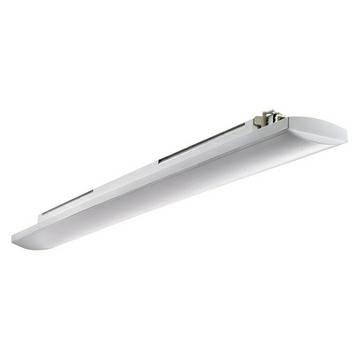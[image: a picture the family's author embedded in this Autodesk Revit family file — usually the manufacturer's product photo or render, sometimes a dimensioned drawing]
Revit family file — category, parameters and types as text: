
# Revit family: Lighting-Industriale-GEWISS-SMART[3]PLUS-PLAFONIERA-LED-EMERGENZA_OPALE_1600mm
name_source: partatom
category: Apparecchi per illuminazione
units: mm (PartAtom-declared; Revit-internal decimal feet)

## family parameters
Condiviso = No
Host = Superficie
Numero OmniClass = 23.80.70.11
Punto di calcolo locali = No
Quota connettore circolare = Usa diametro
Sorgente d'illuminazione = No
Taglio con vuoti quando caricato = No
Tipo di parte = Normale
Titolo OmniClass = Luminaries for Internal Lighting

## types (1)
- Lighting-Industriale-GEWISS-SMART[3]PLUS-PLAFONIERA-LED-EMERGENZA_OPALE_1600mm
    Applicazione = Interno
    Carico apparente = 55 VA
    Catalogo = LIGHTING
    Catalogo Serie = SMART[3] PLUS
    Classe di efficienza LED integrati = A ÷ A++
    Classe isolamento = II
    Codice Electrocod = 2434
    Commenti sul wattaggio = 55W
    Descrizione = SMART3 PLUS 1600 EMERG DT1+DT6 HE OPAL 9 57
    Ganci = GEWISS  - ALLUMINIO
    Garanzia = ND
    Glow Wire Test = 850°C
    Grado di protezione = IP66/IP69
    IDF = 85711e4a-cc34-4edf-afe5-693d24e48af9
    IDT = fc3a2e1b-6a5f-4da6-a0ae-96bfc5d9bbbb
    Immagine tipo = GWS3158P.jpg
    Lampada = LED
    Lampada: = LED
    Lumen output (lm) = 5200
    Lunghezza = 1600 mm
    Lunghezza Lampada = 1600 mm  [stored 5.24934 ft]
    Modello = GWS3325AP957
    Potenza di sistema = 50 W
    Produttore = GEWISS S.p.A.
    Prospetto di default = 1219 mm
    Resistenza agli urti = IK08
    SEO = Plafoniera
    Scheda Tecnica = https://www.gewiss.com
    Schermo = Opale
    Schermo. = Gewiss - Led Acceso
    Stampa 1_100 = Sì
    Stampa 1_200 = No
    Struttura = GEWISS - SMART 3 - GRIGIO
    Temperatura di colore = 5700 K (CRI > 90)
    Temperatura di colore: = 5700 K (CRI > 90)
    Temperatura di funzionamento = ND
    Temperatura di utilizzo = ND
    Tensione = 220-240 V
    Tipologia sorgente luminosa = LED - Non sostituibile
    URL = https://www.gewiss.com
    Versione file RFA = 20.0

note: [stored X ft] marks values corroborated as IEEE doubles in the binary element streams (Revit-internal decimal feet)
